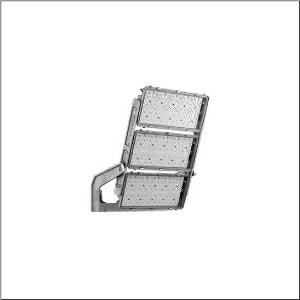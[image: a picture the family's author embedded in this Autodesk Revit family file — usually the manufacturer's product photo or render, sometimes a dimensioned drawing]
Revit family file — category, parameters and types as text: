
# Revit family: floodlight_fl_11_maxi_pro_remote___pl33tblc_5xa779425h01aa_685d
name_source: partatom
category: Lighting Fixtures
units: mm (PartAtom-declared; Revit-internal decimal feet)

## family parameters
Cut with Voids When Loaded = No
Host = Face
Light Source = No
Part Type = Normal
Room Calculation Point = No
Round Connector Dimension = Use Diameter
Shared = No

## types (1)
- --- (1 x LED, 117060 lm, 1335.4 W, 3000K)
    Apparent Load = 1335 VA
    CIE Flux Codes = 24 77 100 100 100
    Color Rendering = 70
    Color Temperature = 3000K
    Default Elevation = 1800 mm
    Description = Floodlight FL 11  maxi  pro Remote floodlight; light control with lens of PMMA; cover panel of toughened safety glass, transparent; light distribution: PL33TBLC, asymmetric direct distribution, LEDcolour temperature: 3000K, colour rendering: CRI > 70, light colour: 730; brightness control: DALI 2 (1 DALI address); with terminal, 8-pole, max. 2.5mm², mains connection: 220..240V/380..400V AC, 50/60Hz, surge voltage resistance: line to ground: 10kV, ECG replaceable separately, LED unit replaceable without ESD environment, dustproof LED module, dimming range 10..100%, no afterglow with DALI off / DMX off command; floodlight with 2x LED unit of diecast aluminium, coated grey; length: 713mm / width: 651mm / height: 338mm; mounting bracket, of diecast aluminium, uncoated, natural, equipment: Power, protection rating (complete): IP66; insulation class (complete): insulation class I (protective earthing); certification: CE, ENEC, VDE; ball protection: ball impact resistance with accessories, rated ambient temperature 10°C, only for outdoor installations, permissible operating ambient temperature: -40..+30°C, permissible storage temperature: -40..+85°C; packaging unit: 1 piece

Light Distribution: PL33TBLC
    Height = 320 mm
    Lamp = 1 x LED
    Lamp Light Flux = 117060 lm
    Lamp Power = 1335.4 W
    Lamp count = 1
    Length = 1002 mm
    Luminous efficacy = 88 lm/W
    Manufacturer = Siteco
    ModVariant = No
    Model = 5XA779425H01AA
    Number of Poles = 1
    OnlyDefault = Yes
    Power Factor = 1
    Product Name = Floodlight FL 11 maxi pro Remote | PL33TBLC
    Product group = floodlight | pylon top
    ProductGroupID = 6101
    Protection Class = Protection class I
    Protection Degree = IP 66
    RLX_Detail_Level = 1
    RlxData = <blob elided: 52053 chars, md5=0aae1ac1>
    Socket = socket
    Standby Power = 0 W
    System Light Flux = 117060 lm
    System Power = 1335 W
    Type Comments = factory setting: luminous flux: 100 % | dim-lin: 254 | 920 mA
    Type Image = l_1006784.jpg
    URL = http://relux.com
    VarID = @adj_005615
    Voltage = 0 V
    Weight = 0.00 kg
    Width = 655 mm

## geometry (parser evidence)
native form markers: Blend x4, Sweep x13
no freeform markers — native parametric forms only
